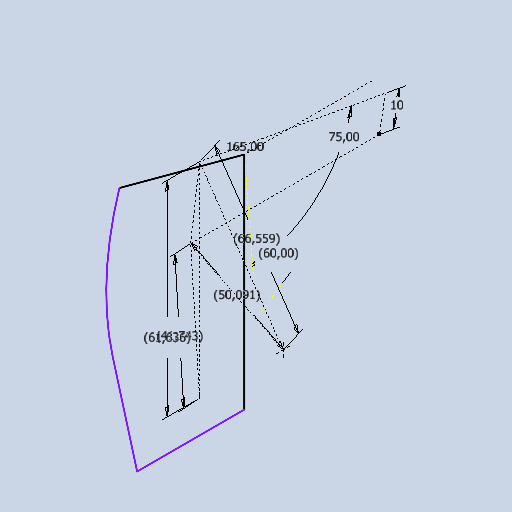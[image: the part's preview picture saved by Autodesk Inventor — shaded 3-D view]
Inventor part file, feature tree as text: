
AUTODESK INVENTOR PART (.ipt)
format: ipt  version: 2025 (Build 290162010, 162A)  size: 96,256 bytes
history: native  units: mm
features: other x4, reference x2, sketch x1
ambient origin geometry x8: Origin, YZ Plane, XZ Plane, XY Plane, X Axis, Y Axis, Z Axis, Center Point
feature tree (7):
  sketch  "Skizze1"  dims[d1=10.472003mm d2=61.63599mm d3=66.559386mm d4=50.091109mm d5=41.742559mm d6=75.0deg d7=10.0mm d8=165.0deg]
  reference  "Referenz2"
  reference  "Referenz3"
  other  "<userpath>\GIT\HDVKBM\CAD\Krandemonstrator\Demonstrator.iam"
  other  "Demonstrator.iam"
  other  "Schlitten:1"
  other  "SchlittenS:1"
